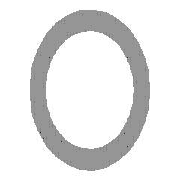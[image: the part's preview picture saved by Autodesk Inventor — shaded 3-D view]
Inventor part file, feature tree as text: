
AUTODESK INVENTOR PART (.ipt)
format: ipt  version: 2021 (Build 250183000, 183)  size: 114,688 bytes
history: native  units: mm (DEFAULTED — no unit token found)
features: other x4, sketch x3, extrude x1, plane x1
ambient origin geometry x8: Origin, YZ Plane, XZ Plane, XY Plane, X Axis, Y Axis, Z Axis, Center Point
bodies: Solid1 (feature_tree)
feature tree (9):
  parser-record x1  (decoder bookkeeping rows leaked as tree rows — omitted from the tree; the rows remain in map.json)
  other  "Driven Length"
  other  "Plano inicial"
  other  "Plano final"
  extrude  "Cuerpo"  Depth=3.556mm
  sketch  "Boceto"  dims[d4=-0.0mm d5=150.0mm d6=90.0deg d7=150.0mm]
  sketch  "Sketch3"  dims[d0=42.164mm d1=3.556mm]
  plane  "Work Plane3"
  sketch  "Sketch4"  dims[d2=150.0mm d3=0.0mm]
